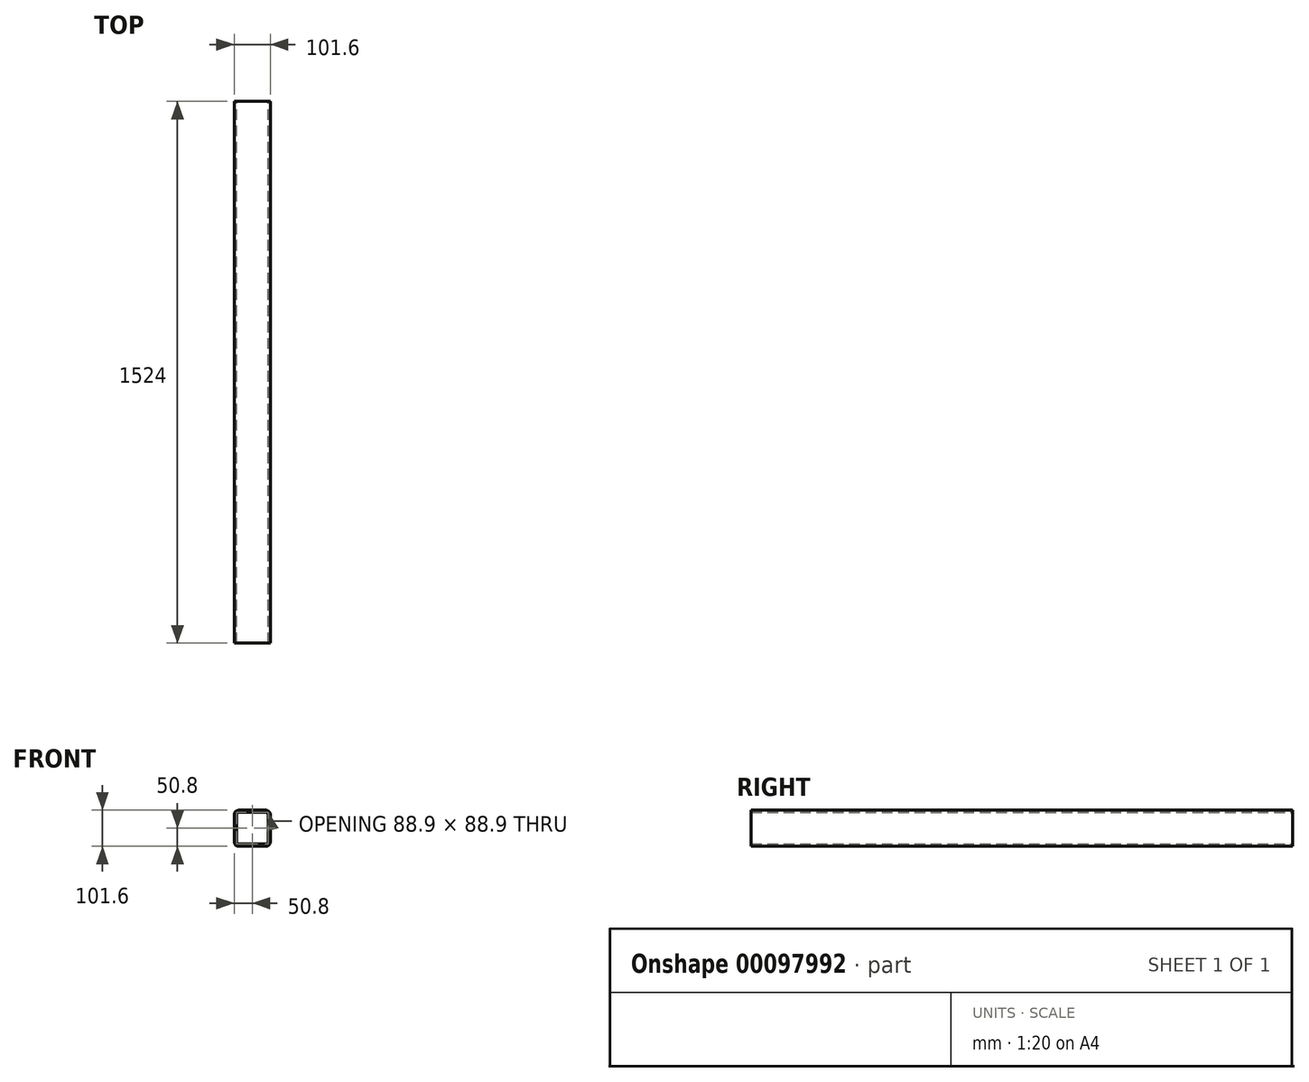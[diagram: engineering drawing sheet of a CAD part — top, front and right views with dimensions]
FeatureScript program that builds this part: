
annotation { "Feature Type Name" : "Feature", "Feature Type Description" : "" }
export const myFeature = defineFeature(function(context is Context, id is Id, definition is map)
    precondition{}
    {
        {
            var Q0;
            Q0=qCreatedBy(makeId("Front.planeOp"),FACE);
            var sketch = newSketch(context, id + "F0", { "sketchPlane" : qUnion([Q0])});
            skLineSegment(sketch, "E0.bottom", {"start": v(38.1, -50.8) * mm, "end": v(-38.1, -50.8) * mm});
            skLineSegment(sketch, "E0.top", {"start": v(38.1, 50.8) * mm, "end": v(-38.1, 50.8) * mm});
            skLineSegment(sketch, "E0.left", {"start": v(50.8, -38.1) * mm, "end": v(50.8, 38.1) * mm});
            skLineSegment(sketch, "E0.right", {"start": v(-50.8, -38.1) * mm, "end": v(-50.8, 38.1) * mm});
            skPoint(sketch, "E0.middle", {"position": v(0, 0) * mm});
            skLineSegment(sketch, "E1.bottom", {"start": v(38.1, -44.45) * mm, "end": v(-38.1, -44.45) * mm});
            skLineSegment(sketch, "E1.top", {"start": v(38.1, 44.45) * mm, "end": v(-38.1, 44.45) * mm});
            skLineSegment(sketch, "E1.left", {"start": v(44.45, -38.1) * mm, "end": v(44.45, 38.1) * mm});
            skLineSegment(sketch, "E1.right", {"start": v(-44.45, -38.1) * mm, "end": v(-44.45, 38.1) * mm});
            skPoint(sketch, "E2.visualSharp", {"position": v(-50.8, 50.8) * mm});
            skArc(sketch, "E2.filletArc", {"start": v(-38.1, 50.8) * mm, "mid": v(-47.08, 47.08) * mm, "end": v(-50.8, 38.1) * mm});
            skPoint(sketch, "E3.visualSharp", {"position": v(50.8, 50.8) * mm});
            skArc(sketch, "E3.filletArc", {"start": v(50.8, 38.1) * mm, "mid": v(47.08, 47.08) * mm, "end": v(38.1, 50.8) * mm});
            skPoint(sketch, "E4.visualSharp", {"position": v(50.8, -50.8) * mm});
            skArc(sketch, "E4.filletArc", {"start": v(38.1, -50.8) * mm, "mid": v(47.08, -47.08) * mm, "end": v(50.8, -38.1) * mm});
            skPoint(sketch, "E5.visualSharp", {"position": v(-50.8, -50.8) * mm});
            skArc(sketch, "E5.filletArc", {"start": v(-50.8, -38.1) * mm, "mid": v(-47.08, -47.08) * mm, "end": v(-38.1, -50.8) * mm});
            skPoint(sketch, "E6.visualSharp", {"position": v(44.45, 44.45) * mm});
            skArc(sketch, "E6.filletArc", {"start": v(44.45, 38.1) * mm, "mid": v(42.6, 42.6) * mm, "end": v(38.1, 44.45) * mm});
            skPoint(sketch, "E7.visualSharp", {"position": v(44.45, -44.45) * mm});
            skArc(sketch, "E7.filletArc", {"start": v(38.1, -44.45) * mm, "mid": v(42.6, -42.6) * mm, "end": v(44.45, -38.1) * mm});
            skPoint(sketch, "E8.visualSharp", {"position": v(-44.45, -44.45) * mm});
            skArc(sketch, "E8.filletArc", {"start": v(-44.45, -38.1) * mm, "mid": v(-42.6, -42.6) * mm, "end": v(-38.1, -44.45) * mm});
            skPoint(sketch, "E9.visualSharp", {"position": v(-44.45, 44.45) * mm});
            skArc(sketch, "E9.filletArc", {"start": v(-38.1, 44.45) * mm, "mid": v(-42.6, 42.6) * mm, "end": v(-44.45, 38.1) * mm});
            skSolve(sketch);
        }
        {
            var Q0;
            Q0=makeQuery(id+"F0.imprint","IMPRINT",FACE,{"disambiguationData":[TD([[makeQuery(id+"F0.imprint","IMPRINT",EDGE,{"derivedFrom":sQuery(id+"F0.wireOp",EDGE,"E0.bottom")}),-1.0]])]});
            extrude(context, id + "F1", {"entities" : qUnion([Q0]), "endBound" : BoundingType.SYMMETRIC, "depth" : 1524 * mm});
        }
    });
